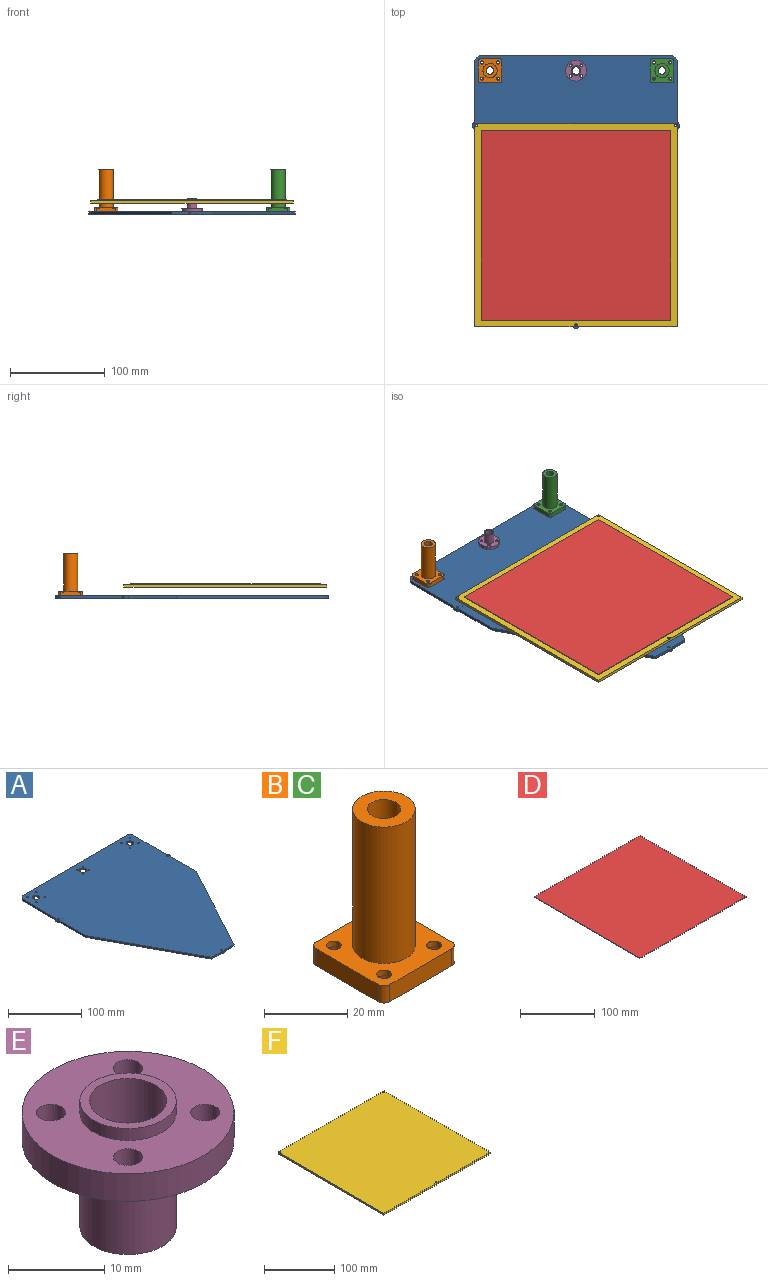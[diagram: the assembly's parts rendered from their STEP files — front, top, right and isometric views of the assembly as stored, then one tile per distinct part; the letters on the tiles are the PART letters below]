
ASSEMBLY  parts=6 mates=5
PART A: 35 faces, bbox 218.2x288x3 mm
  f0: plane 287.99x218.24mm, normal (0,0,1), area 47422.6mm2, adj f2,f3,f4,f5,f6,f7,f8,f9
  f1: plane 287.99x218.24mm, normal (0,0,-1), area 47422.6mm2, adj f2,f3,f4,f5,f6,f7,f8,f9
  f2: plane 65.65x3mm, normal (1,0,0), area 196.9mm2, adj f0,f1,f15,f34
  f3: plane 18.39x3mm, normal (0,-1,0), area 55.2mm2, adj f0,f1,f7,f16
  f4: plane 50.33x3mm, normal (1,0,0), area 151mm2, adj f0,f1,f9,f15
  f5: plane 50.36x3mm, normal (-1,0,0), area 151.1mm2, adj f0,f1,f7,f14
  f6: plane 65.56x3mm, normal (-1,0,0), area 196.7mm2, adj f0,f1,f14,f33
  f7: plane 158.44x85.4mm, normal (-0.88,-0.47,0), area 540mm2, adj f0,f1,f3,f5
  f8: plane 18.39x3mm, normal (0,-1,0), area 55.2mm2, adj f0,f1,f9,f16
  f9: plane 158.44x85.4mm, normal (0.88,-0.47,0), area 540mm2, adj f0,f1,f4,f8
  f10: cylinder r=1.25mm len=3mm, axis (0,0,-1), area 23.6mm2, adj f0,f1
  f11: cylinder r=1.25mm len=3mm, axis (0,0,-1), area 23.6mm2, adj f0,f1
  f12: cylinder r=1.25mm len=3mm, axis (0,0,-1), area 23.6mm2, adj f0,f1
  f13: cylinder r=0.42mm len=3mm, axis (0,0,-1), area 7.8mm2, adj f0,f1
  f14: cylinder r=3.88mm len=6.94mm, axis (0,0,1), area 25.8mm2, adj f0,f1,f5,f6
  f15: cylinder r=3.88mm len=6.89mm, axis (0,0,1), area 25.4mm2, adj f0,f1,f2,f4
  f16: cylinder r=3.88mm len=6.41mm, axis (0,0,1), area 22.6mm2, adj f0,f1,f3,f8
  f17: plane 204x3mm, normal (0,1,0), area 612mm2, adj f0,f1,f33,f34
  f18: cylinder r=1.25mm len=3mm, axis (0,0,1), area 23.6mm2, adj f0,f1
  f19: cylinder r=5mm len=10mm, axis (0,0,1), area 94.2mm2, adj f0,f1
  f20: cylinder r=1.25mm len=3mm, axis (0,0,1), area 23.6mm2, adj f0,f1
  f21: cylinder r=1.25mm len=3mm, axis (0,0,1), area 23.6mm2, adj f0,f1
  f22: cylinder r=1.25mm len=3mm, axis (0,0,1), area 23.6mm2, adj f0,f1
  f23: cylinder r=1.25mm len=3mm, axis (0,0,1), area 23.6mm2, adj f0,f1
  f24: cylinder r=5mm len=10mm, axis (0,0,1), area 94.2mm2, adj f0,f1
  f25: cylinder r=1.25mm len=3mm, axis (0,0,1), area 23.6mm2, adj f0,f1
  f26: cylinder r=1.25mm len=3mm, axis (0,0,1), area 23.6mm2, adj f0,f1
  f27: cylinder r=1.25mm len=3mm, axis (0,0,1), area 23.6mm2, adj f0,f1
  f28: cylinder r=5.25mm len=10.5mm, axis (0,0,1), area 99mm2, adj f0,f1
  f29: cylinder r=1.25mm len=3mm, axis (0,0,1), area 23.6mm2, adj f0,f1
  f30: cylinder r=1.25mm len=3mm, axis (0,0,1), area 23.6mm2, adj f0,f1
  f31: cylinder r=1.25mm len=3mm, axis (0,0,1), area 23.6mm2, adj f0,f1
  f32: cylinder r=1.25mm len=3mm, axis (0,0,1), area 23.6mm2, adj f0,f1
  f33: plane 5x5mm, normal (-0.71,0.71,0), area 21.2mm2, adj f0,f1,f6,f17
  f34: plane 5x5mm, normal (0.71,0.71,0), area 21.2mm2, adj f0,f1,f2,f17
PART B: 25 faces, bbox 25x25x45 mm
  f0: cylinder r=1.75mm len=3.5mm, axis (0,0,-1), area 18.7mm2, adj f13,f21
  f1: cylinder r=1.75mm len=3.5mm, axis (0,0,-1), area 18.7mm2, adj f13,f19
  f2: cylinder r=1.75mm len=3.5mm, axis (0,0,-1), area 18.7mm2, adj f13,f17
  f3: cylinder r=1.75mm len=3.5mm, axis (0,0,-1), area 18.7mm2, adj f13,f15
  f4: plane 21x5mm, normal (0,-1,0), area 105mm2, adj f5,f11,f13,f14
  f5: cylinder r=2mm len=5mm, axis (0,0,-1), area 15.7mm2, adj f4,f6,f13,f14
  f6: plane 21x5mm, normal (1,0,0), area 105mm2, adj f5,f7,f13,f14
  f7: cylinder r=2mm len=5mm, axis (0,0,-1), area 15.7mm2, adj f6,f8,f13,f14
  f8: plane 21x5mm, normal (0,1,0), area 105mm2, adj f7,f9,f13,f14
  f9: cylinder r=2mm len=5mm, axis (0,0,-1), area 15.7mm2, adj f8,f10,f13,f14
  f10: plane 21x5mm, normal (-1,0,0), area 105mm2, adj f9,f11,f13,f14
  f11: cylinder r=2mm len=5mm, axis (0,0,-1), area 15.7mm2, adj f4,f10,f13,f14
  f12: cylinder r=4mm len=45mm, axis (0,0,-1), area 1131mm2, adj f14,f24
  f13: plane 25x25mm, normal (0,0,1), area 406.4mm2, adj f0,f1,f2,f3,f4,f5,f6,f7
  f14: plane 25x25mm, normal (0,0,-1), area 438.6mm2, adj f4,f5,f6,f7,f8,f9,f10,f11
  f15: plane 6.5x6.5mm, normal (0,0,-1), area 23.6mm2, adj f3,f16
  f16: cylinder r=3.25mm len=6.5mm, axis (0,0,-1), area 67.4mm2, adj f14,f15
  f17: plane 6.5x6.5mm, normal (0,0,-1), area 23.6mm2, adj f2,f18
  f18: cylinder r=3.25mm len=6.5mm, axis (0,0,-1), area 67.4mm2, adj f14,f17
  f19: plane 6.5x6.5mm, normal (0,0,-1), area 23.6mm2, adj f1,f20
  f20: cylinder r=3.25mm len=6.5mm, axis (0,0,-1), area 67.4mm2, adj f14,f19
  f21: plane 6.5x6.5mm, normal (0,0,-1), area 23.6mm2, adj f0,f22
  f22: cylinder r=3.25mm len=6.5mm, axis (0,0,-1), area 67.4mm2, adj f14,f21
  f23: cylinder r=7.5mm len=40mm, axis (0,0,-1), area 1885mm2, adj f13,f24
  f24: plane 15x15mm, normal (0,0,1), area 126.4mm2, adj f12,f23
PART C: same geometry as B
PART D: 6 faces, bbox 200x200x0.7 mm
  f0: plane 200x0.7mm, normal (-1,0,0), area 140mm2, adj f1,f3,f4,f5
  f1: plane 200x0.7mm, normal (0,-1,0), area 140mm2, adj f0,f2,f4,f5
  f2: plane 200x0.7mm, normal (1,0,0), area 140mm2, adj f1,f3,f4,f5
  f3: plane 200x0.7mm, normal (0,1,0), area 140mm2, adj f0,f2,f4,f5
  f4: plane 200x200mm, normal (0,0,1), area 40000mm2, adj f0,f1,f2,f3
  f5: plane 200x200mm, normal (0,0,-1), area 40000mm2, adj f0,f1,f2,f3
PART E: 12 faces, bbox 22x22x16 mm
  f0: cylinder r=1.5mm len=3.5mm, axis (0,0,-1), area 33mm2, adj f5,f6
  f1: cylinder r=1.5mm len=3.5mm, axis (0,0,-1), area 33mm2, adj f5,f6
  f2: cylinder r=1.5mm len=3.5mm, axis (0,0,-1), area 33mm2, adj f5,f6
  f3: cylinder r=1.5mm len=3.5mm, axis (0,0,-1), area 33mm2, adj f5,f6
  f4: cylinder r=11mm len=22mm, axis (0,0,-1), area 241.9mm2, adj f5,f6
  f5: plane 22x22mm, normal (0,0,1), area 273.3mm2, adj f0,f1,f2,f3,f4,f9
  f6: plane 22x22mm, normal (0,0,-1), area 273.3mm2, adj f0,f1,f2,f3,f4,f8
  f7: plane 10x10mm, normal (0,0,-1), area 28.3mm2, adj f8,f11
  f8: cylinder r=5mm len=11mm, axis (0,0,1), area 345.6mm2, adj f6,f7
  f9: cylinder r=5mm len=10mm, axis (0,0,1), area 47.1mm2, adj f5,f10
  f10: plane 10x10mm, normal (0,0,1), area 28.3mm2, adj f9,f11
  f11: cylinder r=4mm len=16mm, axis (0,0,-1), area 402.1mm2, adj f7,f10
PART F: 9 faces, bbox 214x214x3 mm
  f0: plane 214x214mm, normal (0,0,1), area 45781.3mm2, adj f2,f3,f4,f5,f6,f7,f8
  f1: plane 214x214mm, normal (0,0,-1), area 45781.3mm2, adj f2,f3,f4,f5,f6,f7,f8
  f2: plane 214x3mm, normal (1,0,0), area 642mm2, adj f0,f1,f7,f8
  f3: plane 214x3mm, normal (-1,0,0), area 642mm2, adj f0,f1,f7,f8
  f4: cylinder r=1.25mm len=3mm, axis (0,0,-1), area 23.6mm2, adj f0,f1
  f5: cylinder r=1.25mm len=3mm, axis (0,0,-1), area 23.6mm2, adj f0,f1
  f6: cylinder r=1.25mm len=3mm, axis (0,0,-1), area 23.6mm2, adj f0,f1
  f7: plane 214x3mm, normal (0,-1,0), area 642mm2, adj f0,f1,f2,f3
  f8: plane 214x3mm, normal (0,1,0), area 642mm2, adj f0,f1,f2,f3
PLACE A t=(-59.7,-51.89,-4.71)mm
PLACE B t=(-150.89,91.1,-1.71)mm
PLACE C t=(30.53,91.1,-1.71)mm
PLACE D t=(-59.7,-51.9,7.29)mm
PLACE E rot(axis=(1,0,0),180deg) t=(-60.18,91.1,1.79)mm
PLACE F t=(-59.7,-51.89,7.29)mm
MATE fastened F.f6 <-> A.f12  axis (0,0,-1) through (-60.18,-177.01,7.29)mm
MATE fastened C.f3 <-> A.f23  axis (0,0,-1) through (39.02,99.58,-1.71)mm
MATE fastened E.f0 <-> A.f30  axis (0,0,-1) through (-54.52,96.75,-1.71)mm
MATE fastened D.f5 <-> F.f0  axis (0,0,-1) through (-60.18,-72.14,10.29)mm
MATE fastened B.f3 <-> A.f27  axis (0,0,-1) through (-142.4,99.58,-1.71)mm
